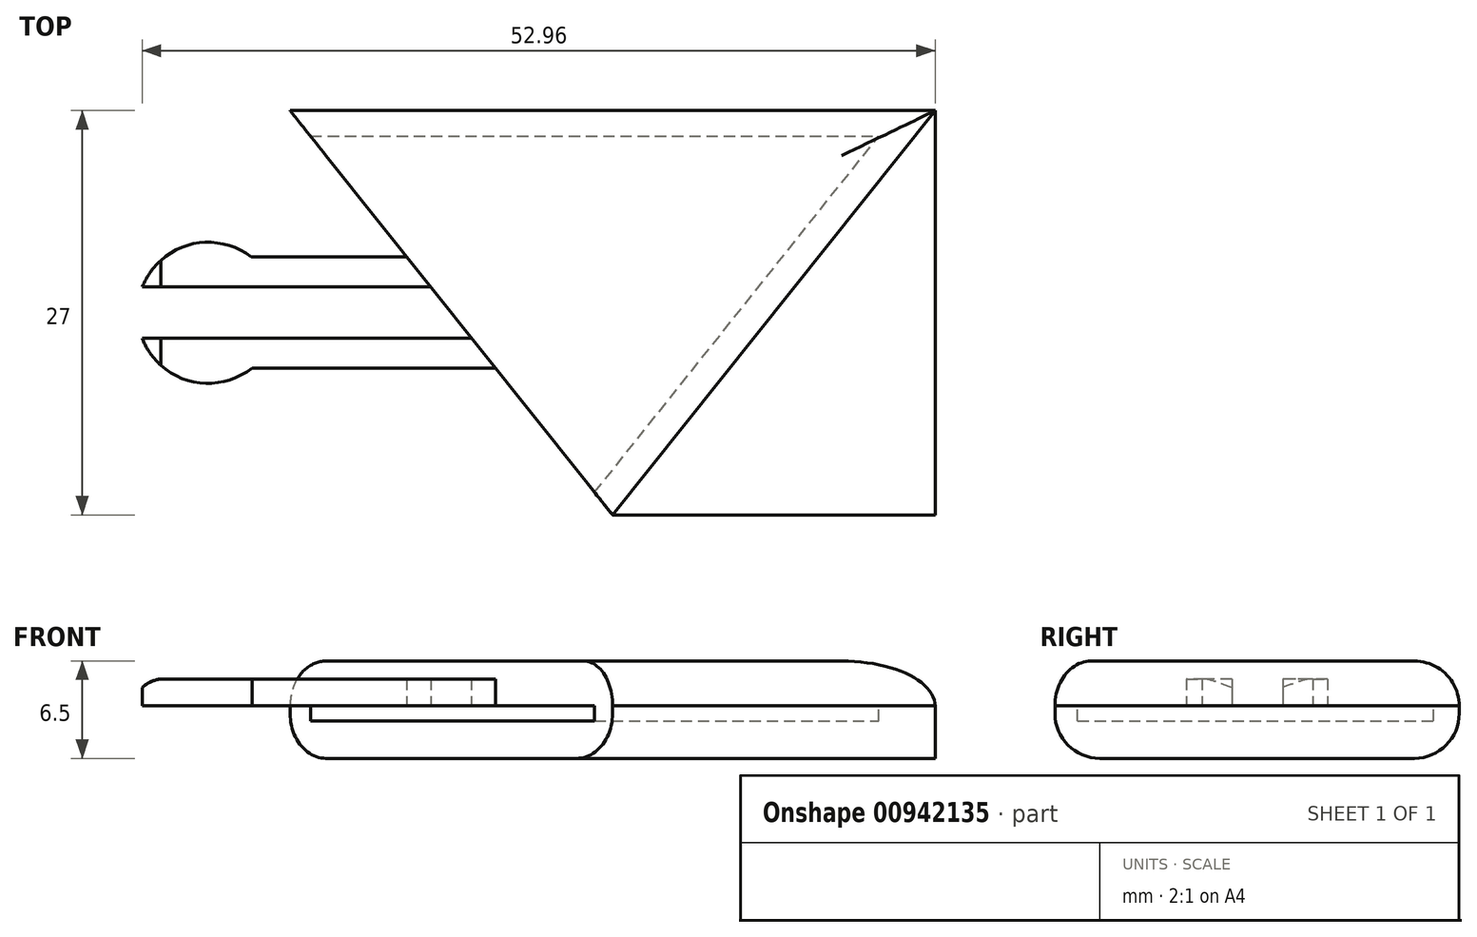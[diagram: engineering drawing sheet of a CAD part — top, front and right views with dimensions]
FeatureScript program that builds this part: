
annotation { "Feature Type Name" : "Feature", "Feature Type Description" : "" }
export const myFeature = defineFeature(function(context is Context, id is Id, definition is map)
    precondition{}
    {
        {
            var Q0;
            Q0=qCreatedBy(makeId("Top.planeOp"),FACE);
            var sketch = newSketch(context, id + "F0", { "sketchPlane" : qUnion([Q0])});
            skCircle(sketch, "E0", {"center": v(0, 0) * mm, "radius": 5 * mm, "construction": true});
            skLineSegment(sketch, "E1", {"start": v(3, 4) * mm, "end": v(13.09, 4) * mm, "construction": true});
            skLineSegment(sketch, "E2", {"start": v(3, -4) * mm, "end": v(19.42, -4) * mm, "construction": true});
            skLineSegment(sketch, "E3", {"start": v(19.42, -4) * mm, "end": v(13.09, 4) * mm, "construction": true});
            skLineSegment(sketch, "E4.MirrorCS", {"start": v(27.02, -13.5) * mm, "end": v(-5.48, -13.5) * mm, "construction": true});
            skLineSegment(sketch, "E5.MirrorCS", {"start": v(5.48, 13.5) * mm, "end": v(27.02, -13.5) * mm, "construction": true});
            skLineSegment(sketch, "E6.MirrorCS", {"start": v(-27.02, 13.5) * mm, "end": v(5.48, 13.5) * mm, "construction": true});
            skLineSegment(sketch, "E7.MirrorCS", {"start": v(-27.02, 13.5) * mm, "end": v(-5.48, -13.5) * mm, "construction": true});
            skLineSegment(sketch, "E8", {"start": v(5.48, 13.5) * mm, "end": v(48.56, 13.5) * mm, "construction": true});
            skLineSegment(sketch, "E9", {"start": v(48.56, 13.5) * mm, "end": v(27.02, -13.5) * mm, "construction": true});
            skLineSegment(sketch, "E10", {"start": v(6.85, 11.79) * mm, "end": v(44.8, 11.79) * mm, "construction": true});
            skLineSegment(sketch, "E11", {"start": v(44.8, 11.79) * mm, "end": v(25.82, -12) * mm, "construction": true});
            skSolve(sketch);
        }
        {
            var Q0;
            Q0=qCreatedBy(makeId("Top.planeOp"),FACE);
            var sketch = newSketch(context, id + "F1", { "sketchPlane" : qUnion([Q0])});
            skCircle(sketch, "E12", {"center": v(0, 0) * mm, "radius": 5 * mm, "construction": true});
            skLineSegment(sketch, "E13", {"start": v(3, 4) * mm, "end": v(13.09, 4) * mm, "construction": true});
            skLineSegment(sketch, "E14", {"start": v(3, -4) * mm, "end": v(19.42, -4) * mm, "construction": true});
            skLineSegment(sketch, "E15", {"start": v(19.42, -4) * mm, "end": v(13.09, 4) * mm, "construction": true});
            skLineSegment(sketch, "E16.MirrorCS", {"start": v(27.02, -13.5) * mm, "end": v(-5.48, -13.5) * mm, "construction": true});
            skLineSegment(sketch, "E17.MirrorCS", {"start": v(5.48, 13.5) * mm, "end": v(27.02, -13.5) * mm, "construction": true});
            skLineSegment(sketch, "E18.MirrorCS", {"start": v(-27.02, 13.5) * mm, "end": v(5.48, 13.5) * mm, "construction": true});
            skLineSegment(sketch, "E19.MirrorCS", {"start": v(-27.02, 13.5) * mm, "end": v(-5.48, -13.5) * mm, "construction": true});
            skLineSegment(sketch, "E20", {"start": v(5.48, 13.5) * mm, "end": v(48.56, 13.5) * mm, "construction": true});
            skLineSegment(sketch, "E21", {"start": v(48.56, 13.5) * mm, "end": v(27.02, -13.5) * mm, "construction": true});
            skLineSegment(sketch, "E22", {"start": v(6.85, 11.79) * mm, "end": v(44.8, 11.79) * mm, "construction": true});
            skLineSegment(sketch, "E23", {"start": v(44.8, 11.79) * mm, "end": v(25.82, -12) * mm, "construction": true});
            skLineSegment(sketch, "E24", {"start": v(5.48, 13.5) * mm, "end": v(27.02, -13.5) * mm});
            skLineSegment(sketch, "E25", {"start": v(48.56, 13.5) * mm, "end": v(5.48, 13.5) * mm});
            skLineSegment(sketch, "E26", {"start": v(48.56, 13.5) * mm, "end": v(27.02, -13.5) * mm});
            skLineSegment(sketch, "E27", {"start": v(27.02, -13.5) * mm, "end": v(48.56, -13.5) * mm});
            skLineSegment(sketch, "E28", {"start": v(48.56, -13.5) * mm, "end": v(48.56, 13.5) * mm});
            skSolve(sketch);
        }
        {
            var Q0;
            Q0=makeQuery(id+"F1.imprint","IMPRINT",FACE,{"disambiguationData":[TD([[makeQuery(id+"F1.imprint","IMPRINT",EDGE,{"derivedFrom":sQuery(id+"F1.wireOp",EDGE,"E24")}),1.0]])]});
            var Q1;
            Q1=makeQuery(id+"F1.imprint","IMPRINT",FACE,{"disambiguationData":[TD([[makeQuery(id+"F1.imprint","IMPRINT",EDGE,{"derivedFrom":sQuery(id+"F1.wireOp",EDGE,"E26")}),1.0]])]});
            extrude(context, id + "F2", {"entities" : qUnion([Q0, Q1]), "oppositeDirection" : true, "depth" : 3.5 * mm, "offsetDistance" : 25 * mm});
        }
        {
            var Q0;
            Q0=qCreatedBy(makeId("Top.planeOp"),FACE);
            var sketch = newSketch(context, id + "F3", { "sketchPlane" : qUnion([Q0])});
            skCircle(sketch, "E29", {"center": v(0, 0) * mm, "radius": 5 * mm, "construction": true});
            skLineSegment(sketch, "E30", {"start": v(3, 4) * mm, "end": v(13.09, 4) * mm, "construction": true});
            skLineSegment(sketch, "E31", {"start": v(3, -4) * mm, "end": v(19.42, -4) * mm, "construction": true});
            skLineSegment(sketch, "E32", {"start": v(19.42, -4) * mm, "end": v(13.09, 4) * mm, "construction": true});
            skLineSegment(sketch, "E33.MirrorCS", {"start": v(27.02, -13.5) * mm, "end": v(-5.48, -13.5) * mm, "construction": true});
            skLineSegment(sketch, "E34.MirrorCS", {"start": v(5.48, 13.5) * mm, "end": v(27.02, -13.5) * mm, "construction": true});
            skLineSegment(sketch, "E35.MirrorCS", {"start": v(-27.02, 13.5) * mm, "end": v(5.48, 13.5) * mm, "construction": true});
            skLineSegment(sketch, "E36.MirrorCS", {"start": v(-27.02, 13.5) * mm, "end": v(-5.48, -13.5) * mm, "construction": true});
            skLineSegment(sketch, "E37", {"start": v(5.48, 13.5) * mm, "end": v(48.56, 13.5) * mm, "construction": true});
            skLineSegment(sketch, "E38", {"start": v(48.56, 13.5) * mm, "end": v(27.02, -13.5) * mm, "construction": true});
            skLineSegment(sketch, "E39", {"start": v(6.85, 11.79) * mm, "end": v(44.8, 11.79) * mm, "construction": true});
            skLineSegment(sketch, "E40", {"start": v(44.8, 11.79) * mm, "end": v(25.82, -12) * mm, "construction": true});
            skLineSegment(sketch, "E41", {"start": v(6.85, 11.79) * mm, "end": v(44.8, 11.79) * mm});
            skLineSegment(sketch, "E42", {"start": v(25.82, -12) * mm, "end": v(44.8, 11.79) * mm});
            skLineSegment(sketch, "E43", {"start": v(25.82, -12) * mm, "end": v(6.85, 11.79) * mm});
            skLineSegment(sketch, "E44", {"start": v(27.02, -13.5) * mm, "end": v(48.56, 13.5) * mm});
            skLineSegment(sketch, "E45", {"start": v(48.56, -13.5) * mm, "end": v(27.02, -13.5) * mm});
            skSolve(sketch);
        }
        {
            var Q0;
            Q0=makeQuery(id+"F3.imprint","IMPRINT",FACE,{"disambiguationData":[TD([[makeQuery(id+"F3.imprint","IMPRINT",EDGE,{"derivedFrom":sQuery(id+"F3.wireOp",EDGE,"E41")}),-1.0]])]});
            extrude(context, id + "F4", {"entities" : qUnion([Q0]), "operationType" : NewBodyOperationType.REMOVE, "oppositeDirection" : true, "depth" : 1 * mm, "offsetDistance" : 25 * mm});
        }
        {
            var Q0;
            Q0=makeQuery(id+"F2.opExtrude","CAP_FACE",FACE,{"disambiguationData":[OSD([sQuery(id+"F1.wireOp",EDGE,"E24"),sQuery(id+"F1.wireOp",EDGE,"E25"),sQuery(id+"F1.wireOp",EDGE,"E26")])],"isStart":true});
            var sketch = newSketch(context, id + "F5", { "sketchPlane" : qUnion([Q0])});
            skCircle(sketch, "E46", {"center": v(0, 0) * mm, "radius": 5 * mm, "construction": true});
            skLineSegment(sketch, "E47", {"start": v(3, 4) * mm, "end": v(13.09, 4) * mm, "construction": true});
            skLineSegment(sketch, "E48", {"start": v(3, -4) * mm, "end": v(19.42, -4) * mm, "construction": true});
            skLineSegment(sketch, "E49", {"start": v(19.42, -4) * mm, "end": v(13.09, 4) * mm, "construction": true});
            skLineSegment(sketch, "E50.MirrorCS", {"start": v(27.02, -13.5) * mm, "end": v(-5.48, -13.5) * mm, "construction": true});
            skLineSegment(sketch, "E51.MirrorCS", {"start": v(5.48, 13.5) * mm, "end": v(27.02, -13.5) * mm, "construction": true});
            skLineSegment(sketch, "E52.MirrorCS", {"start": v(-27.02, 13.5) * mm, "end": v(5.48, 13.5) * mm, "construction": true});
            skLineSegment(sketch, "E53.MirrorCS", {"start": v(-27.02, 13.5) * mm, "end": v(-5.48, -13.5) * mm, "construction": true});
            skLineSegment(sketch, "E54", {"start": v(5.48, 13.5) * mm, "end": v(48.56, 13.5) * mm, "construction": true});
            skLineSegment(sketch, "E55", {"start": v(48.56, 13.5) * mm, "end": v(27.02, -13.5) * mm, "construction": true});
            skLineSegment(sketch, "E56", {"start": v(6.85, 11.79) * mm, "end": v(44.8, 11.79) * mm, "construction": true});
            skLineSegment(sketch, "E57", {"start": v(44.8, 11.79) * mm, "end": v(25.82, -12) * mm, "construction": true});
            skCircle(sketch, "E58", {"center": v(0, 0) * mm, "radius": 4.71 * mm});
            skLineSegment(sketch, "E59", {"start": v(2.88, 3.73) * mm, "end": v(13.28, 3.73) * mm});
            skLineSegment(sketch, "E60", {"start": v(2.93, -3.69) * mm, "end": v(19.2, -3.69) * mm});
            skLineSegment(sketch, "E61", {"start": v(9.17, -3.69) * mm, "end": v(9.17, -1.69) * mm, "construction": true});
            skLineSegment(sketch, "E62", {"start": v(8.08, 3.73) * mm, "end": v(8.08, 1.73) * mm, "construction": true});
            skLineSegment(sketch, "E63", {"start": v(14.87, 1.73) * mm, "end": v(4.38, 1.73) * mm});
            skLineSegment(sketch, "E64", {"start": v(4.38, 1.73) * mm, "end": v(-4.38, 1.73) * mm});
            skLineSegment(sketch, "E65", {"start": v(17.6, -1.69) * mm, "end": v(4.4, -1.69) * mm});
            skLineSegment(sketch, "E66", {"start": v(4.4, -1.69) * mm, "end": v(-4.4, -1.69) * mm});
            skLineSegment(sketch, "E67", {"start": v(13.28, 3.73) * mm, "end": v(5.48, 13.5) * mm});
            skLineSegment(sketch, "E68", {"start": v(48.56, 13.5) * mm, "end": v(27.02, -13.5) * mm});
            skLineSegment(sketch, "E69", {"start": v(19.2, -3.69) * mm, "end": v(27.02, -13.5) * mm});
            skLineSegment(sketch, "E70", {"start": v(14.87, 1.73) * mm, "end": v(17.6, -1.69) * mm});
            skLineSegment(sketch, "E71", {"start": v(27.02, -13.5) * mm, "end": v(48.56, 13.5) * mm});
            skLineSegment(sketch, "E72", {"start": v(48.56, -13.5) * mm, "end": v(27.02, -13.5) * mm});
            skSolve(sketch);
        }
        {
            var Q0;
            {var subQ2=sQuery(id+"F5.wireOp",EDGE,"E59");Q0=makeQuery(id+"F5.imprint","IMPRINT",FACE,{"disambiguationData":[TD([[makeQuery(id+"F5.imprint","IMPRINT",EDGE,{"derivedFrom":subQ2}),-1.0]])]});}
            var Q1;
            {var subQ2=sQuery(id+"F5.wireOp",EDGE,"E68");Q1=makeQuery(id+"F5.imprint","IMPRINT",FACE,{"disambiguationData":[TD([[makeQuery(id+"F5.imprint","IMPRINT",EDGE,{"derivedFrom":subQ2}),-1.0]])]});}
            var Q2;
            {var subQ2=sQuery(id+"F5.wireOp",EDGE,"E64");Q2=makeQuery(id+"F5.imprint","IMPRINT",FACE,{"disambiguationData":[TD([[makeQuery(id+"F5.imprint","IMPRINT",EDGE,{"derivedFrom":subQ2}),-1.0]])]});}
            var Q3;
            {var subQ2=sQuery(id+"F5.wireOp",EDGE,"E66");Q3=makeQuery(id+"F5.imprint","IMPRINT",FACE,{"disambiguationData":[TD([[makeQuery(id+"F5.imprint","IMPRINT",EDGE,{"derivedFrom":subQ2}),1.0]])]});}
            var Q4;
            Q4=makeQuery(id+"F5.imprint","IMPRINT",FACE,{"disambiguationData":[TD([[makeQuery(id+"F5.imprint","IMPRINT",EDGE,{"derivedFrom":sQuery(id+"F5.wireOp",EDGE,"E71")}),-1.0]])]});
            var Q5;
            {var subQ1=sQuery(id+"F5.wireOp",EDGE,"E71");Q5=makeQuery(id+"F5.imprint","IMPRINT",FACE,{"disambiguationData":[TD([[makeQuery(id+"F5.imprint","IMPRINT",EDGE,{"derivedFrom":subQ1}),1.0]])]});}
            extrude(context, id + "F6", {"entities" : qUnion([Q0, Q1, Q2, Q3, Q4, Q5]), "operationType" : NewBodyOperationType.ADD, "depth" : 1.8 * mm, "offsetDistance" : 25 * mm});
        }
        {
            var Q0;
            Q0=makeQuery(id+"F6.opExtrude","CAP_FACE",FACE,{"disambiguationData":[OSD([sQuery(id+"F1.wireOp",EDGE,"E25"),sQuery(id+"F5.wireOp",EDGE,"E58"),sQuery(id+"F5.wireOp",EDGE,"E59"),sQuery(id+"F5.wireOp",EDGE,"E60"),sQuery(id+"F5.wireOp",EDGE,"E63"),sQuery(id+"F5.wireOp",EDGE,"E64"),sQuery(id+"F5.wireOp",EDGE,"E65"),sQuery(id+"F5.wireOp",EDGE,"E66"),sQuery(id+"F5.wireOp",EDGE,"E67"),sQuery(id+"F5.wireOp",EDGE,"E68"),sQuery(id+"F5.wireOp",EDGE,"E69"),sQuery(id+"F5.wireOp",EDGE,"E70")])],"isStart":false});
            var sketch = newSketch(context, id + "F7", { "sketchPlane" : qUnion([Q0])});
            skCircle(sketch, "E73", {"center": v(0, 0) * mm, "radius": 5 * mm, "construction": true});
            skLineSegment(sketch, "E74", {"start": v(3, 4) * mm, "end": v(13.09, 4) * mm, "construction": true});
            skLineSegment(sketch, "E75", {"start": v(3, -4) * mm, "end": v(19.42, -4) * mm, "construction": true});
            skLineSegment(sketch, "E76", {"start": v(19.42, -4) * mm, "end": v(13.09, 4) * mm, "construction": true});
            skLineSegment(sketch, "E77.MirrorCS", {"start": v(27.02, -13.5) * mm, "end": v(-5.48, -13.5) * mm, "construction": true});
            skLineSegment(sketch, "E78.MirrorCS", {"start": v(5.48, 13.5) * mm, "end": v(27.02, -13.5) * mm, "construction": true});
            skLineSegment(sketch, "E79.MirrorCS", {"start": v(-27.02, 13.5) * mm, "end": v(5.48, 13.5) * mm, "construction": true});
            skLineSegment(sketch, "E80.MirrorCS", {"start": v(-27.02, 13.5) * mm, "end": v(-5.48, -13.5) * mm, "construction": true});
            skLineSegment(sketch, "E81", {"start": v(5.48, 13.5) * mm, "end": v(48.56, 13.5) * mm, "construction": true});
            skLineSegment(sketch, "E82", {"start": v(48.56, 13.5) * mm, "end": v(27.02, -13.5) * mm, "construction": true});
            skLineSegment(sketch, "E83", {"start": v(6.85, 11.79) * mm, "end": v(44.8, 11.79) * mm, "construction": true});
            skLineSegment(sketch, "E84", {"start": v(44.8, 11.79) * mm, "end": v(25.82, -12) * mm, "construction": true});
            skLineSegment(sketch, "E85", {"start": v(5.48, 13.5) * mm, "end": v(27.02, -13.5) * mm});
            skLineSegment(sketch, "E86", {"start": v(48.56, 13.5) * mm, "end": v(5.48, 13.5) * mm});
            skSolve(sketch);
        }
        {
            var Q0;
            {var subQ4=sQuery(id+"F7.wireOp",EDGE,"E86");Q0=makeQuery(id+"F7.imprint","IMPRINT",FACE,{"disambiguationData":[TD([[makeQuery(id+"F7.imprint","IMPRINT",EDGE,{"derivedFrom":subQ4}),1.0]])]});}
            extrude(context, id + "F8", {"entities" : qUnion([Q0]), "operationType" : NewBodyOperationType.ADD, "depth" : 1.2 * mm, "offsetDistance" : 25 * mm});
        }
        {
            var Q0;
            Q0=makeQuery(id+"F8.opExtrude","CAP_EDGE",EDGE,{"disambiguationData":[OSD([sQuery(id+"F7.wireOp",EDGE,"E86")])],"isStart":false});
            var Q1;
            Q1=makeQuery(id+"F2.opExtrude","CAP_EDGE",EDGE,{"disambiguationData":[OSD([sQuery(id+"F1.wireOp",EDGE,"E25")])],"isStart":false});
            var Q2;
            Q2=makeQuery(id+"F8.opExtrude","CAP_EDGE",EDGE,{"disambiguationData":[OSD([sQuery(id+"F5.wireOp",EDGE,"E68")])],"isStart":false});
            var Q3;
            Q3=makeQuery(id+"F2.opExtrude","CAP_EDGE",EDGE,{"disambiguationData":[OSD([sQuery(id+"F1.wireOp",EDGE,"E26")])],"isStart":false});
            var Q4;
            Q4=makeQuery(id+"F8.opExtrude","CAP_EDGE",EDGE,{"disambiguationData":[OSD([sQuery(id+"F5.wireOp",EDGE,"E72")])],"isStart":false});
            var Q5;
            Q5=makeQuery(id+"F2.opExtrude","CAP_EDGE",EDGE,{"disambiguationData":[OSD([sQuery(id+"F1.wireOp",EDGE,"E27")])],"isStart":false});
            fillet(context, id + "F9", {"entities" : qUnion([Q0, Q1, Q2, Q3, Q4, Q5]), "radius" : 3 * mm, "tangentPropagation" : true, "allowEdgeOverflow" : false});
        }
        {
            var Q0;
            Q0=makeQuery(id+"F6.opExtrude","SWEPT_FACE",FACE,{"disambiguationData":[OSD([sQuery(id+"F5.wireOp",EDGE,"E60")])]});
            var sketch = newSketch(context, id + "F10", { "sketchPlane" : qUnion([Q0])});
            skArc(sketch, "E87", {"start": v(-2.83, 1.82) * mm, "mid": v(-3.7, 1.67) * mm, "end": v(-4.43, 1.2) * mm});
            skLineSegment(sketch, "E88", {"start": v(-2.83, 1.82) * mm, "end": v(-4.43, 1.82) * mm});
            skLineSegment(sketch, "E89", {"start": v(-4.43, 1.82) * mm, "end": v(-4.43, 1.2) * mm});
            skSolve(sketch);
        }
        {
            var Q0;
            {var subQ0=sQuery(id+"F10.wireOp",EDGE,"E89");Q0=makeQuery(id+"F10.imprint","IMPRINT",FACE,{"disambiguationData":[TD([[makeQuery(id+"F10.imprint","IMPRINT",EDGE,{"derivedFrom":subQ0}),1.0]])]});}
            extrude(context, id + "F11", {"entities" : qUnion([Q0]), "operationType" : NewBodyOperationType.REMOVE, "endBound" : BoundingType.THROUGH_ALL, "oppositeDirection" : true, "depth" : 25 * mm, "offsetDistance" : 25 * mm});
        }
    });
